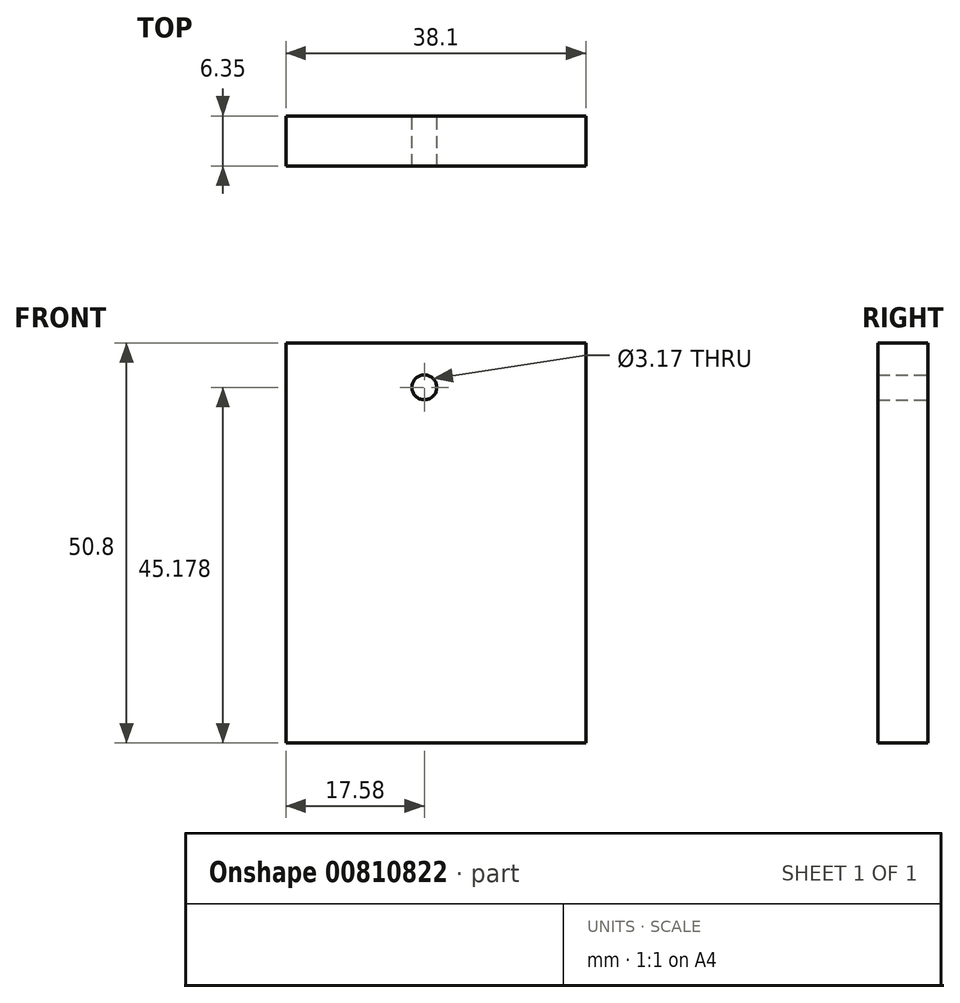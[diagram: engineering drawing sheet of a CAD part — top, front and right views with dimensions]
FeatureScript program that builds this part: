
annotation { "Feature Type Name" : "Feature", "Feature Type Description" : "" }
export const myFeature = defineFeature(function(context is Context, id is Id, definition is map)
    precondition{}
    {
        {
            var Q0;
            Q0=qCreatedBy(makeId("Front.planeOp"),FACE);
            var sketch = newSketch(context, id + "F0", { "sketchPlane" : qUnion([Q0])});
            skLineSegment(sketch, "E0.bottom", {"start": v(-17.58, 3.18) * mm, "end": v(20.52, 3.18) * mm});
            skLineSegment(sketch, "E0.top", {"start": v(-17.58, -47.62) * mm, "end": v(20.52, -47.62) * mm});
            skLineSegment(sketch, "E0.left", {"start": v(-17.58, 3.18) * mm, "end": v(-17.58, -47.62) * mm});
            skLineSegment(sketch, "E0.right", {"start": v(20.52, 3.17) * mm, "end": v(20.52, -47.62) * mm});
            skPoint(sketch, "E1.center.orphan", {"position": v(0, 3.58) * mm});
            skCircle(sketch, "E2", {"center": v(0, -2.44) * mm, "radius": 1.59 * mm});
            skSolve(sketch);
        }
        {
            var Q0;
            Q0 = qSketchRegion(id + "F0", true);
            extrude(context, id + "F1", {"entities" : qUnion([Q0]), "depth" : 6.35 * mm, "offsetDistance" : 25.4 * mm});
        }
    });
